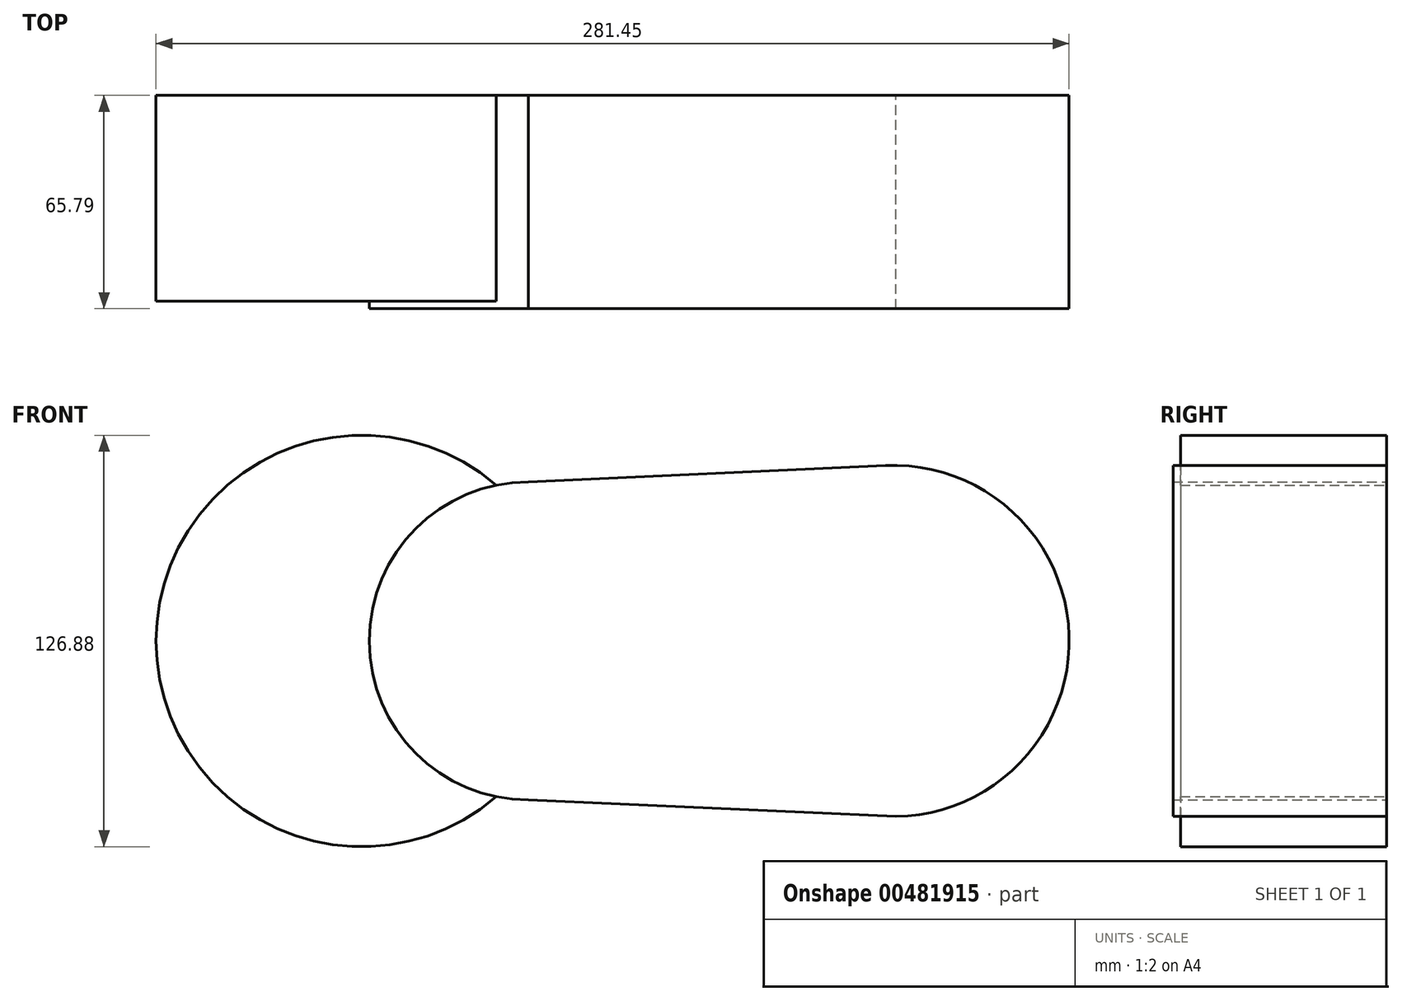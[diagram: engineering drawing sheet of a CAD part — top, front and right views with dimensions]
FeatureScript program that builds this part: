
annotation { "Feature Type Name" : "Feature", "Feature Type Description" : "" }
export const myFeature = defineFeature(function(context is Context, id is Id, definition is map)
    precondition{}
    {
        {
            var Q0;
            Q0=qCreatedBy(makeId("Front.planeOp"),FACE);
            var sketch = newSketch(context, id + "F0", { "sketchPlane" : qUnion([Q0])});
            skCircle(sketch, "E0", {"center": v(0, 0) * mm, "radius": 49.04 * mm});
            skCircle(sketch, "E1", {"center": v(112.54, 0) * mm, "radius": 54.15 * mm});
            skLineSegment(sketch, "E2", {"start": v(0, 49.04) * mm, "end": v(110.05, 54.1) * mm});
            skLineSegment(sketch, "E3", {"start": v(0, -49.04) * mm, "end": v(113.31, -54.15) * mm});
            skSolve(sketch);
        }
        {
            var Q0;
            {var subQ0=sQuery(id+"F0.wireOp",EDGE,"E3");var subQ1=sQuery(id+"F0.wireOp",EDGE,"E1");var subQ2=makeQuery(id+"F0.imprint","INTERSECT",VERTEX,{"disambiguationData":[OD(0.0)],"derivedFrom":[subQ1,subQ0]});Q0=makeQuery(id+"F0.imprint","IMPRINT",FACE,{"disambiguationData":[TD([[makeQuery(id+"F0.imprint","IMPRINT",EDGE,{"disambiguationData":[TD([[subQ2,1.0]])],"derivedFrom":subQ1}),1.0]])]});}
            var Q1;
            {var subQ0=sQuery(id+"F0.wireOp",EDGE,"E2");Q1=makeQuery(id+"F0.imprint","IMPRINT",FACE,{"disambiguationData":[TD([[makeQuery(id+"F0.imprint","IMPRINT",EDGE,{"derivedFrom":subQ0}),-1.0]])]});}
            var Q2;
            {var subQ0=sQuery(id+"F0.wireOp",EDGE,"E0");var subQ1=makeQuery(id+"F0.imprint","INTERSECT",VERTEX,{"derivedFrom":[subQ0,sQuery(id+"F0.wireOp",EDGE,"E2")]});Q2=makeQuery(id+"F0.imprint","IMPRINT",FACE,{"disambiguationData":[TD([[makeQuery(id+"F0.imprint","IMPRINT",EDGE,{"disambiguationData":[TD([[subQ1,-1.0]])],"derivedFrom":subQ0}),1.0]])]});}
            extrude(context, id + "F1", {"entities" : qUnion([Q0, Q1, Q2]), "depth" : 65.8 * mm});
        }
        {
            var Q0;
            Q0=qCreatedBy(makeId("Front.planeOp"),FACE);
            var sketch = newSketch(context, id + "F2", { "sketchPlane" : qUnion([Q0])});
            skCircle(sketch, "E4", {"center": v(98.02, 0) * mm, "radius": 38.11 * mm});
            skCircle(sketch, "E5", {"center": v(-51.31, 0) * mm, "radius": 63.44 * mm});
            skSolve(sketch);
        }
        {
            var Q0;
            Q0 = qSketchRegion(id + "F2", true);
            extrude(context, id + "F3", {"entities" : qUnion([Q0]), "operationType" : NewBodyOperationType.ADD, "depth" : 63.5 * mm});
        }
    });
